# Revit family: UM314 Banco Olea
name_source: partatom
category: Mobiliario
units: mm (PartAtom-declared; Revit-internal decimal feet)

## family parameters
Compartido = No
Corte con vacíos al cargar = No
Número OmniClass = 23.40.20.00
Punto de cálculo de habitación = No
Se basa en plano de trabajo = No
Siempre vertical = Sí
Título OmniClass = General Furniture and Specialties

## types (1)
- UM314 Banco Olea
    Acabado Listones = Autoclave vacío-presión clase 4 contra la carcoma, termitas e insectos.
    Acabado bancada = Acero corten
    Accessibilidad = Sí
    Altura asiento = 450 mm  [stored 1.47638 ft]
    Altura total = 754 mm  [stored 2.47375 ft]
    Ancho = 518 mm  [stored 1.69948 ft]
    Comentarios de tipo = Pies tubulares de acero corten de 50 x 100 mm. Tablones de sección 210 x 50 mm en madera de pino tratada en autoclave vacíopresión clase 4 contra la carcoma, termitas e insectos. Tornillería de acero inoxidable.
    Fabricante = BENITO
    Ficha tecnica = http://www.benito.com
    Instalación = Anclaje recomendado: Tornillos M10 roscados a las bancadas y embebidos en hormigón.Tornillos no suministrados.
    Largo = 1850 mm  [stored 6.06955 ft]
    Material bancada = Acero corten
    Material listones = Madera de pino
    Modelo = Banco Olea
    Referencia = UM314
    URL = http://www.benito.com
    URL Producto = http://www.benito.com

note: [stored X ft] marks values corroborated as IEEE doubles in the binary element streams (Revit-internal decimal feet)

## geometry (parser evidence)
native form markers: Blend x4
no freeform markers — native parametric forms only
